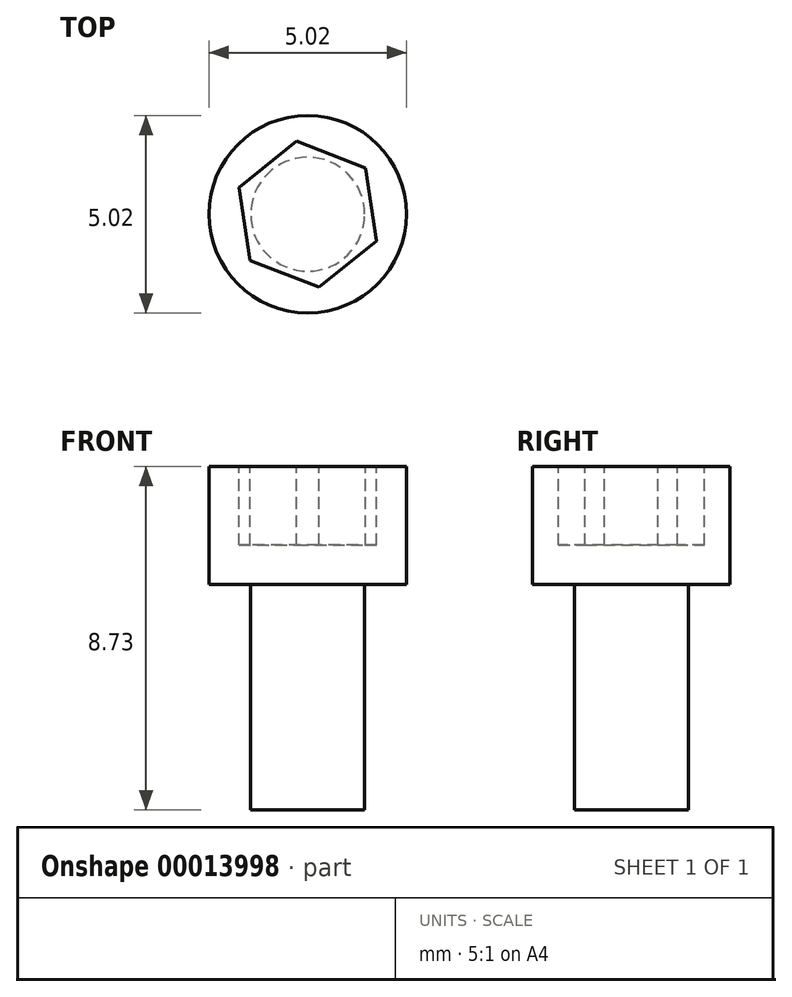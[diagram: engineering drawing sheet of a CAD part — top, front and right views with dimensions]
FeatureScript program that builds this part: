
annotation { "Feature Type Name" : "Feature", "Feature Type Description" : "" }
export const myFeature = defineFeature(function(context is Context, id is Id, definition is map)
    precondition{}
    {
        {
            var Q0;
            Q0=qCreatedBy(makeId("Top.planeOp"),FACE);
            var sketch = newSketch(context, id + "F0", { "sketchPlane" : qUnion([Q0])});
            skCircle(sketch, "E0", {"center": v(0, 0) * mm, "radius": 2.5 * mm});
            skCircle(sketch, "E1", {"center": v(0, 0) * mm, "radius": 1.45 * mm});
            skSolve(sketch);
        }
        {
            var Q0;
            Q0=makeQuery(id+"F0.imprint","IMPRINT",FACE,{"disambiguationData":[TD([[makeQuery(id+"F0.imprint","IMPRINT",EDGE,{"derivedFrom":sQuery(id+"F0.wireOp",EDGE,"E0")}),1.0]])]});
            var Q1;
            Q1=makeQuery(id+"F0.imprint","IMPRINT",FACE,{"disambiguationData":[TD([[makeQuery(id+"F0.imprint","IMPRINT",EDGE,{"derivedFrom":sQuery(id+"F0.wireOp",EDGE,"E1")}),1.0]])]});
            extrude(context, id + "F1", {"entities" : qUnion([Q0, Q1]), "depth" : 3 * mm});
        }
        {
            var Q0;
            Q0=makeQuery(id+"F0.imprint","IMPRINT",FACE,{"disambiguationData":[TD([[makeQuery(id+"F0.imprint","IMPRINT",EDGE,{"derivedFrom":sQuery(id+"F0.wireOp",EDGE,"E1")}),1.0]])]});
            extrude(context, id + "F2", {"entities" : qUnion([Q0]), "operationType" : NewBodyOperationType.ADD, "oppositeDirection" : true, "depth" : 5.73 * mm});
        }
        {
            var Q0;
            Q0=makeQuery(id+"F1.opExtrude","CAP_FACE",FACE,{"disambiguationData":[OSD([sQuery(id+"F0.wireOp",EDGE,"E0")])],"isStart":false});
            var sketch = newSketch(context, id + "F3", { "sketchPlane" : qUnion([Q0])});
            skPoint(sketch, "E2.0", {"position": v(0, 0) * mm});
            skCircle(sketch, "E3.cCircle", {"center": v(0, 0) * mm, "radius": 1.62 * mm, "construction": true});
            skLineSegment(sketch, "E3.0", {"start": v(-0.28, 1.85) * mm, "end": v(1.46, 1.17) * mm});
            skLineSegment(sketch, "E3.1", {"start": v(1.46, 1.17) * mm, "end": v(1.75, -0.68) * mm});
            skLineSegment(sketch, "E3.2", {"start": v(1.75, -0.68) * mm, "end": v(0.28, -1.85) * mm});
            skLineSegment(sketch, "E3.3", {"start": v(0.28, -1.85) * mm, "end": v(-1.46, -1.17) * mm});
            skLineSegment(sketch, "E3.4", {"start": v(-1.46, -1.17) * mm, "end": v(-1.75, 0.68) * mm});
            skLineSegment(sketch, "E3.5", {"start": v(-1.75, 0.68) * mm, "end": v(-0.28, 1.85) * mm});
            skPoint(sketch, "E3.0.midPoint", {"position": v(0.6, 1.51) * mm});
            skSolve(sketch);
        }
        {
            var Q0;
            Q0=makeQuery(id+"F3.imprint","IMPRINT",FACE,{"disambiguationData":[TD([[makeQuery(id+"F3.imprint","IMPRINT",EDGE,{"derivedFrom":sQuery(id+"F3.wireOp",EDGE,"E3.0")}),-1.0]])]});
            extrude(context, id + "F4", {"entities" : qUnion([Q0]), "operationType" : NewBodyOperationType.REMOVE, "oppositeDirection" : true, "depth" : 2 * mm});
        }
    });
